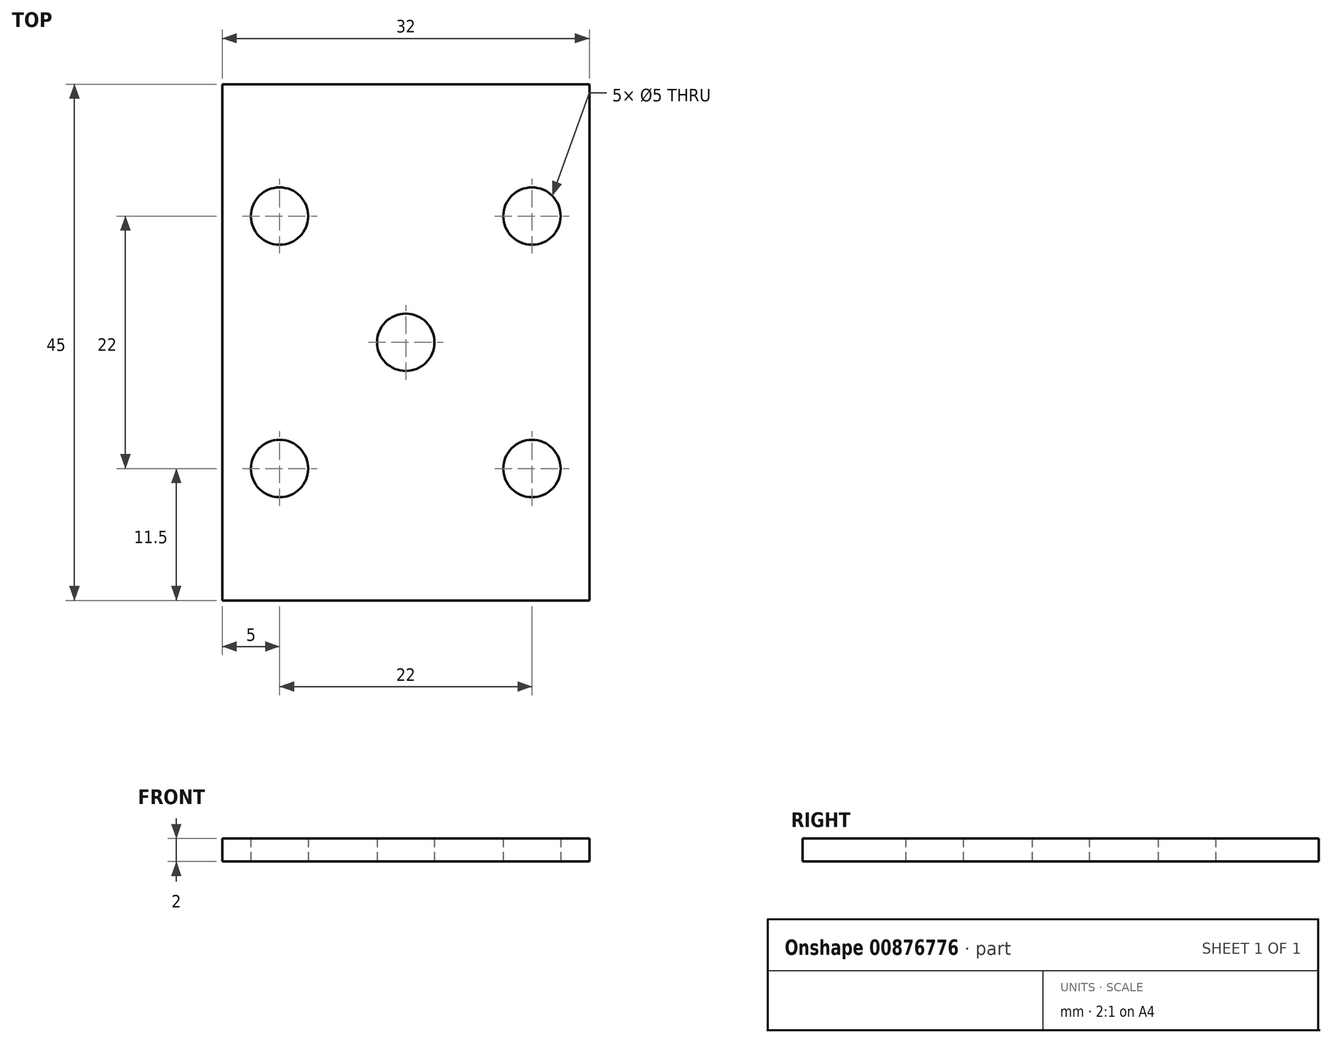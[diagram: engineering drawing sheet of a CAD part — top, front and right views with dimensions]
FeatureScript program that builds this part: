
annotation { "Feature Type Name" : "Feature", "Feature Type Description" : "" }
export const myFeature = defineFeature(function(context is Context, id is Id, definition is map)
    precondition{}
    {
        {
            var Q0;
            Q0=qCreatedBy(makeId("Top.planeOp"),FACE);
            var sketch = newSketch(context, id + "F0", { "sketchPlane" : qUnion([Q0])});
            skLineSegment(sketch, "E0.bottom", {"start": v(-16, 22.5) * mm, "end": v(16, 22.5) * mm});
            skLineSegment(sketch, "E0.top", {"start": v(-16, -22.5) * mm, "end": v(16, -22.5) * mm});
            skLineSegment(sketch, "E0.left", {"start": v(-16, 22.5) * mm, "end": v(-16, -22.5) * mm});
            skLineSegment(sketch, "E0.right", {"start": v(16, 22.5) * mm, "end": v(16, -22.5) * mm});
            skPoint(sketch, "E0.middle", {"position": v(0, 0) * mm});
            skCircle(sketch, "E1", {"center": v(0, 0) * mm, "radius": 2.5 * mm});
            skCircle(sketch, "E2", {"center": v(-11, 11) * mm, "radius": 2.5 * mm});
            skCircle(sketch, "E3", {"center": v(11, 11) * mm, "radius": 2.5 * mm});
            skCircle(sketch, "E4", {"center": v(11, -11) * mm, "radius": 2.5 * mm});
            skCircle(sketch, "E5", {"center": v(-11, -11) * mm, "radius": 2.5 * mm});
            skSolve(sketch);
        }
        {
            var Q0;
            Q0=makeQuery(id+"F0.imprint","IMPRINT",FACE,{"disambiguationData":[TD([[makeQuery(id+"F0.imprint","IMPRINT",EDGE,{"derivedFrom":sQuery(id+"F0.wireOp",EDGE,"E0.bottom")}),-1.0]])]});
            extrude(context, id + "F1", {"entities" : qUnion([Q0]), "depth" : 2 * mm, "offsetDistance" : 25 * mm});
        }
    });
